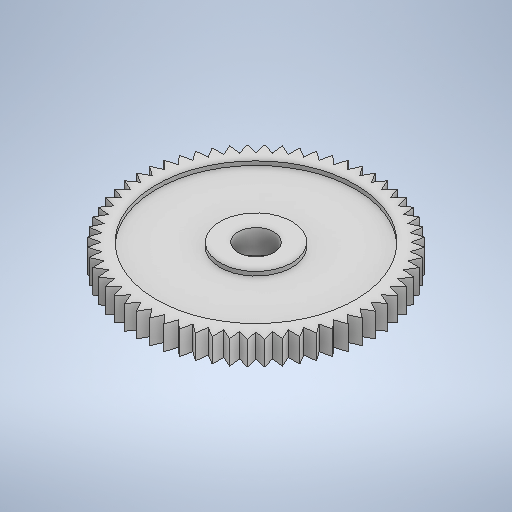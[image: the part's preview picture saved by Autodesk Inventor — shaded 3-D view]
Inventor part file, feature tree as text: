
AUTODESK INVENTOR PART (.ipt)
format: ipt  version: 2025.2 (Build 292293000, 293)  size: 405,504 bytes
history: native  units: mm
features: extrude x3, sketch x3, pattern_circular x1
ambient origin geometry x8: Origin, YZ Plane, XZ Plane, XY Plane, X Axis, Y Axis, Z Axis, Center Point
bodies: Solid1 (feature_tree)
feature tree (7):
  extrude  "Extrusion1"  Depth=45.0mm
  extrude  "Extrusion3"  Depth=4.5mm
  extrude  "Extrusion4"  Depth=2.5mm
  pattern_circular  "Circular Pattern2"  [2 undecoded]
  sketch  "Sketch1"  dims[d0=50.0mm d1=45.0mm]
  sketch  "Sketch3"  dims[d2=4.5mm d3=20.0mm]
  sketch  "Sketch4"  dims[d4=20.0mm d5=5.0mm d6=5.0mm d7=5.0mm d8=5.0mm d9=2.0mm d10=0.0mm d22=9.0mm d23=0.5mm d24=2.5mm d25=0.0mm d26=0.0mm d29=25.0mm d31=30.0mm d32=2.0mm d33=30.0deg d34=2.0mm d35=30.0deg d36=0.5mm d37=2.5mm d38=0.0mm d39=0.0mm d40=600.0mm d41=360.0deg]
note: 2 required parameter values undecoded (feature->parameter linkage not recoverable at this tier; creation-order binding heuristic only, values carry confidence <= 0.55)
